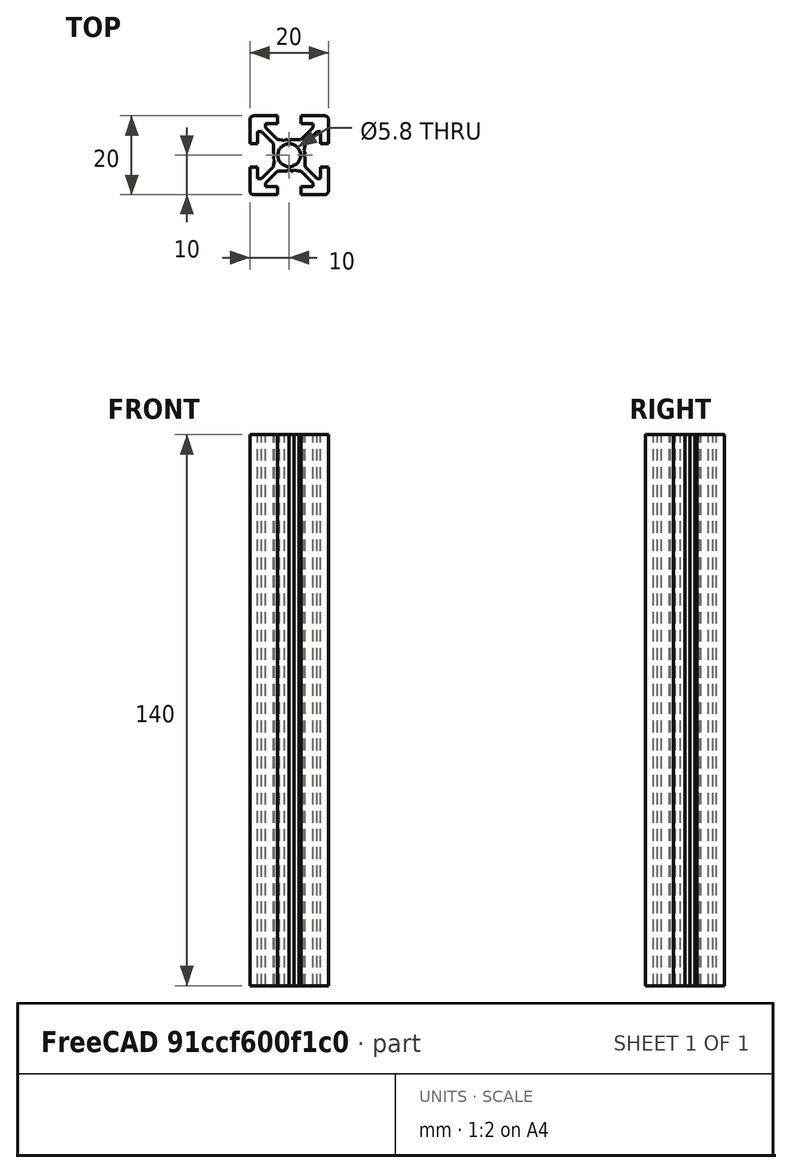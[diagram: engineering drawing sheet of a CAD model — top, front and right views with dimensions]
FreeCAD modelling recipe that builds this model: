
FCSTD DOCUMENT  (FreeCAD 0.17R13519 (Git))
Label: Z_Profile_2020_bed_back
License: All rights reserved
LicenseURL: http://en.wikipedia.org/wiki/All_rights_reserved
objects: Sketcher::SketchObject×1, PartDesign::Pad×1, PartDesign::Body×1
note: 4 computed .brp shape members not serialized (recipe doc carries the construction recipe); baked Part::Feature solids carry a one-line shape summary decoded from their .brp

FEATURE [Sketcher::SketchObject] Sketch001
  MapMode = 4
  sketch-geometry (77):
    g0: LineSegment StartX=-8 StartY=-3 StartZ=0 EndX=-10 EndY=-3 EndZ=0
    g1: LineSegment StartX=-10 StartY=-3 StartZ=0 EndX=-10 EndY=-9 EndZ=0
    g2: ArcOfCircle CenterX=-9 CenterY=-9 CenterZ=0 NormalX=0 NormalY=0 NormalZ=1 AngleXU=0 Radius=1 StartAngle=3.14159 EndAngle=4.71239
    g3: LineSegment StartX=-9 StartY=-10 StartZ=0 EndX=-3 EndY=-10 EndZ=0
    g4: LineSegment StartX=-3 StartY=-10 StartZ=0 EndX=-3 EndY=-8 EndZ=0
    g5: LineSegment StartX=-3 StartY=-8 StartZ=0 EndX=-6 EndY=-8 EndZ=0
    g6: LineSegment StartX=-6 StartY=-8 StartZ=0 EndX=-6 EndY=-7.06066 EndZ=0
    g7: LineSegment StartX=-6 StartY=-7.06066 StartZ=0 EndX=-2.93934 EndY=-4 EndZ=0
    g8: LineSegment StartX=-2.93934 StartY=-4 StartZ=0 EndX=-0.65359 EndY=-4 EndZ=0
    g9: ArcOfCircle CenterX=-0.65359 CenterY=-3.5 CenterZ=0 NormalX=0 NormalY=0 NormalZ=1 AngleXU=0 Radius=0.5 StartAngle=4.71239 EndAngle=5.23599
    g10: LineSegment StartX=-0.40359 StartY=-3.93301 StartZ=0 EndX=0 EndY=-3.7 EndZ=0
    g11: LineSegment StartX=0 StartY=-3.7 StartZ=0 EndX=0.40359 EndY=-3.93301 EndZ=0
    g12: ArcOfCircle CenterX=0.65359 CenterY=-3.5 CenterZ=0 NormalX=0 NormalY=0 NormalZ=1 AngleXU=0 Radius=0.5 StartAngle=4.18879 EndAngle=5.23599
    g13: LineSegment StartX=0.90359 StartY=-3.93301 StartZ=0 EndX=1.21889 EndY=-3.75098 EndZ=0
    g14: LineSegment StartX=1.21889 StartY=-3.75098 StartZ=0 EndX=2.5 EndY=-4 EndZ=0
    g15: LineSegment StartX=2.5 StartY=-4 StartZ=0 EndX=2.93934 EndY=-4 EndZ=0
    g16: LineSegment StartX=2.93934 StartY=-4 StartZ=0 EndX=6 EndY=-7.06066 EndZ=0
    g17: LineSegment StartX=6 StartY=-7.06066 StartZ=0 EndX=6 EndY=-8 EndZ=0
    g18: LineSegment StartX=6 StartY=-8 StartZ=0 EndX=3 EndY=-8 EndZ=0
    g19: LineSegment StartX=3 StartY=-8 StartZ=0 EndX=3 EndY=-10 EndZ=0
    g20: LineSegment StartX=3 StartY=-10 StartZ=0 EndX=9 EndY=-10 EndZ=0
    g21: ArcOfCircle CenterX=9 CenterY=-9 CenterZ=0 NormalX=0 NormalY=0 NormalZ=1 AngleXU=0 Radius=1 StartAngle=4.71239 EndAngle=6.28319
    g22: LineSegment StartX=10 StartY=-9 StartZ=0 EndX=10 EndY=-3 EndZ=0
    g23: LineSegment StartX=10 StartY=-3 StartZ=0 EndX=8 EndY=-3 EndZ=0
    g24: LineSegment StartX=8 StartY=-3 StartZ=0 EndX=8 EndY=-6 EndZ=0
    g25: LineSegment StartX=8 StartY=-6 StartZ=0 EndX=7.06066 EndY=-6 EndZ=0
    g26: LineSegment StartX=7.06066 StartY=-6 StartZ=0 EndX=4 EndY=-2.93934 EndZ=0
    g27: LineSegment StartX=4 StartY=-2.93934 StartZ=0 EndX=4 EndY=-0.65359 EndZ=0
    g28: ArcOfCircle CenterX=3.5 CenterY=-0.65359 CenterZ=0 NormalX=0 NormalY=0 NormalZ=1 AngleXU=0 Radius=0.5 StartAngle=0 EndAngle=0.523599
    g29: LineSegment StartX=3.93301 StartY=-0.40359 StartZ=0 EndX=3.7 EndY=0 EndZ=0
    g30: LineSegment StartX=3.7 StartY=0 StartZ=0 EndX=3.93301 EndY=0.40359 EndZ=0
    g31: ArcOfCircle CenterX=3.5 CenterY=0.65359 CenterZ=0 NormalX=0 NormalY=0 NormalZ=1 AngleXU=0 Radius=0.5 StartAngle=5.75959 EndAngle=6.80678
    g32: LineSegment StartX=3.93301 StartY=0.90359 StartZ=0 EndX=3.75098 EndY=1.21889 EndZ=0
    g33: LineSegment StartX=3.75098 StartY=1.21889 StartZ=0 EndX=4 EndY=2.5 EndZ=0
    g34: LineSegment StartX=4 StartY=2.5 StartZ=0 EndX=4 EndY=2.93934 EndZ=0
    g35: LineSegment StartX=4 StartY=2.93934 StartZ=0 EndX=7.06066 EndY=6 EndZ=0
    g36: LineSegment StartX=7.06066 StartY=6 StartZ=0 EndX=8 EndY=6 EndZ=0
    g37: LineSegment StartX=8 StartY=6 StartZ=0 EndX=8 EndY=3 EndZ=0
    g38: LineSegment StartX=8 StartY=3 StartZ=0 EndX=10 EndY=3 EndZ=0
    g39: LineSegment StartX=10 StartY=3 StartZ=0 EndX=10 EndY=9 EndZ=0
    g40: ArcOfCircle CenterX=9 CenterY=9 CenterZ=0 NormalX=0 NormalY=0 NormalZ=1 AngleXU=0 Radius=1 StartAngle=0 EndAngle=1.5708
    g41: LineSegment StartX=9 StartY=10 StartZ=0 EndX=3 EndY=10 EndZ=0
    g42: LineSegment StartX=3 StartY=10 StartZ=0 EndX=3 EndY=8 EndZ=0
    g43: LineSegment StartX=3 StartY=8 StartZ=0 EndX=6 EndY=8 EndZ=0
    g44: LineSegment StartX=6 StartY=8 StartZ=0 EndX=6 EndY=7.06066 EndZ=0
    g45: LineSegment StartX=6 StartY=7.06066 StartZ=0 EndX=2.93934 EndY=4 EndZ=0
    g46: LineSegment StartX=2.93934 StartY=4 StartZ=0 EndX=0.65359 EndY=4 EndZ=0
    g47: ArcOfCircle CenterX=0.65359 CenterY=3.5 CenterZ=0 NormalX=0 NormalY=0 NormalZ=1 AngleXU=0 Radius=0.5 StartAngle=1.5708 EndAngle=2.0944
    g48: LineSegment StartX=0.40359 StartY=3.93301 StartZ=0 EndX=0 EndY=3.7 EndZ=0
    g49: LineSegment StartX=0 StartY=3.7 StartZ=0 EndX=-0.40359 EndY=3.93301 EndZ=0
    g50: ArcOfCircle CenterX=-0.65359 CenterY=3.5 CenterZ=0 NormalX=0 NormalY=0 NormalZ=1 AngleXU=0 Radius=0.5 StartAngle=1.0472 EndAngle=2.0944
    g51: LineSegment StartX=-0.90359 StartY=3.93301 StartZ=0 EndX=-1.21889 EndY=3.75098 EndZ=0
    g52: LineSegment StartX=-1.21889 StartY=3.75098 StartZ=0 EndX=-2.5 EndY=4 EndZ=0
    g53: LineSegment StartX=-2.5 StartY=4 StartZ=0 EndX=-2.93934 EndY=4 EndZ=0
    g54: LineSegment StartX=-2.93934 StartY=4 StartZ=0 EndX=-6 EndY=7.06066 EndZ=0
    g55: LineSegment StartX=-6 StartY=7.06066 StartZ=0 EndX=-6 EndY=8 EndZ=0
    g56: LineSegment StartX=-6 StartY=8 StartZ=0 EndX=-3 EndY=8 EndZ=0
    g57: LineSegment StartX=-3 StartY=8 StartZ=0 EndX=-3 EndY=10 EndZ=0
    g58: LineSegment StartX=-3 StartY=10 StartZ=0 EndX=-9 EndY=10 EndZ=0
    g59: ArcOfCircle CenterX=-9 CenterY=9 CenterZ=0 NormalX=0 NormalY=0 NormalZ=1 AngleXU=0 Radius=1 StartAngle=1.5708 EndAngle=3.14159
    g60: LineSegment StartX=-10 StartY=9 StartZ=0 EndX=-10 EndY=3 EndZ=0
    g61: LineSegment StartX=-10 StartY=3 StartZ=0 EndX=-8 EndY=3 EndZ=0
    g62: LineSegment StartX=-8 StartY=3 StartZ=0 EndX=-8 EndY=6 EndZ=0
    g63: LineSegment StartX=-8 StartY=6 StartZ=0 EndX=-7.06066 EndY=6 EndZ=0
    g64: LineSegment StartX=-7.06066 StartY=6 StartZ=0 EndX=-4 EndY=2.93934 EndZ=0
    g65: LineSegment StartX=-4 StartY=2.93934 StartZ=0 EndX=-4 EndY=0.65359 EndZ=0
    g66: ArcOfCircle CenterX=-3.5 CenterY=0.65359 CenterZ=0 NormalX=0 NormalY=0 NormalZ=1 AngleXU=0 Radius=0.5 StartAngle=3.14159 EndAngle=3.66519
    g67: LineSegment StartX=-3.93301 StartY=0.40359 StartZ=0 EndX=-3.7 EndY=0 EndZ=0
    g68: LineSegment StartX=-3.7 StartY=0 StartZ=0 EndX=-3.93301 EndY=-0.40359 EndZ=0
    g69: ArcOfCircle CenterX=-3.5 CenterY=-0.65359 CenterZ=0 NormalX=0 NormalY=0 NormalZ=1 AngleXU=0 Radius=0.5 StartAngle=2.61799 EndAngle=3.66519
    g70: LineSegment StartX=-3.93301 StartY=-0.90359 StartZ=0 EndX=-3.75098 EndY=-1.21889 EndZ=0
    g71: LineSegment StartX=-3.75098 StartY=-1.21889 StartZ=0 EndX=-4 EndY=-2.5 EndZ=0
    g72: LineSegment StartX=-4 StartY=-2.5 StartZ=0 EndX=-4 EndY=-2.93934 EndZ=0
    g73: LineSegment StartX=-4 StartY=-2.93934 StartZ=0 EndX=-7.06066 EndY=-6 EndZ=0
    g74: LineSegment StartX=-7.06066 StartY=-6 StartZ=0 EndX=-8 EndY=-6 EndZ=0
    g75: LineSegment StartX=-8 StartY=-6 StartZ=0 EndX=-8 EndY=-3 EndZ=0
    g76: Circle CenterX=0 CenterY=0 CenterZ=0 NormalX=0 NormalY=0 NormalZ=1 AngleXU=0 Radius=2.9
  constraints (105):
    c: Horizontal(g0)
    c: Coincident(g0,g1)
    c: Vertical(g1)
    c: Coincident(g1,g2)
    c: Coincident(g2,g3)
    c: Horizontal(g3)
    c: Coincident(g3,g4)
    c: Coincident(g4,g5)
    c: Horizontal(g5)
    c: Coincident(g5,g6)
    c: Coincident(g6,g7)
    c: Coincident(g7,g8)
    c: Horizontal(g8)
    c: Coincident(g8,g9)
    c: Coincident(g9,g10)
    c: Coincident(g10,g11)
    c: Coincident(g11,g12)
    c: Coincident(g12,g13)
    c: Coincident(g13,g14)
    c: Coincident(g14,g15)
    c: Horizontal(g15)
    c: Coincident(g15,g16)
    c: Coincident(g16,g17)
    c: Coincident(g17,g18)
    c: Coincident(g18,g19)
    c: Vertical(g19)
    c: Coincident(g19,g20)
    c: Horizontal(g20)
    c: Coincident(g20,g21)
    c: Coincident(g21,g22)
    c: Vertical(g22)
    c: Coincident(g22,g23)
    c: Horizontal(g23)
    c: Coincident(g23,g24)
    c: Vertical(g24)
    c: Coincident(g24,g25)
    c: Coincident(g25,g26)
    c: Coincident(g26,g27)
    c: Vertical(g27)
    c: Coincident(g27,g28)
    c: Coincident(g28,g29)
    c: Coincident(g29,g30)
    c: Coincident(g30,g31)
    c: Coincident(g31,g32)
    c: Coincident(g32,g33)
    c: Coincident(g33,g34)
    c: Vertical(g34)
    c: Coincident(g34,g35)
    c: Coincident(g35,g36)
    c: Coincident(g36,g37)
    c: Coincident(g37,g38)
    c: Horizontal(g38)
    c: Coincident(g38,g39)
    c: Vertical(g39)
    c: Coincident(g39,g40)
    c: Coincident(g40,g41)
    c: Horizontal(g41)
    c: Coincident(g41,g42)
    c: Coincident(g42,g43)
    c: Horizontal(g43)
    c: Coincident(g43,g44)
    c: Coincident(g44,g45)
    c: Coincident(g45,g46)
    c: Horizontal(g46)
    c: Coincident(g46,g47)
    c: Coincident(g47,g48)
    c: Coincident(g48,g49)
    c: Coincident(g49,g50)
    c: Coincident(g50,g51)
    c: Coincident(g51,g52)
    c: Coincident(g52,g53)
    c: Horizontal(g53)
    c: Coincident(g53,g54)
    c: Coincident(g54,g55)
    c: Vertical(g55)
    c: Coincident(g55,g56)
    c: Coincident(g56,g57)
    c: Vertical(g57)
    c: Coincident(g57,g58)
    c: Horizontal(g58)
    c: Coincident(g58,g59)
    c: Coincident(g59,g60)
    c: Vertical(g60)
    c: Coincident(g60,g61)
    c: Horizontal(g61)
    c: Coincident(g61,g62)
    c: Vertical(g62)
    c: Coincident(g62,g63)
    c: Horizontal(g63)
    c: Coincident(g63,g64)
    c: Coincident(g64,g65)
    c: Vertical(g65)
    c: Coincident(g65,g66)
    c: Coincident(g66,g67)
    c: Coincident(g67,g68)
    c: Coincident(g68,g69)
    c: Coincident(g69,g70)
    c: Coincident(g70,g71)
    c: Coincident(g71,g72)
    c: Vertical(g72)
    c: Coincident(g72,g73)
    c: Coincident(g73,g74)
    c: Coincident(g74,g75)
    c: Coincident(g75,g0)
    c: Radius(g76) = 2.9
FEATURE [PartDesign::Pad] Pad
  Length = 140
  Length2 = 100
  Midplane = true
  Profile = -> Sketch001
  Type = 0
FEATURE [PartDesign::Body] Body
  Group = -> [Sketch001,Pad]
  Origin = -> Origin
  Tip = -> Pad
